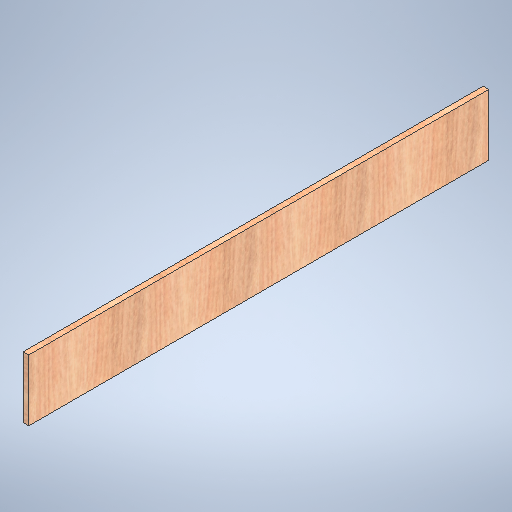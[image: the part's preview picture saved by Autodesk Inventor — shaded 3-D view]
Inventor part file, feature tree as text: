
AUTODESK INVENTOR PART (.ipt)
format: ipt  version: 2025.1 (Build 291241020, 241B)  size: 329,216 bytes
history: native  units: in
note: dims shown in document units (in); Inventor stores cm internally (conversion verified against a paired STEP export)
features: extrude x1, sketch x1
ambient origin geometry x8: Origin, YZ Plane, XZ Plane, XY Plane, X Axis, Y Axis, Z Axis, Center Point
bodies: Solid1 (feature_tree)
feature tree (2):
  extrude  "Extrusion1"  Depth=0.5in TaperAngle=0.0deg
  sketch  "Sketch1"  dims[d1=41.25in d2=0.5in d3=0.0in d4=5.5in]
